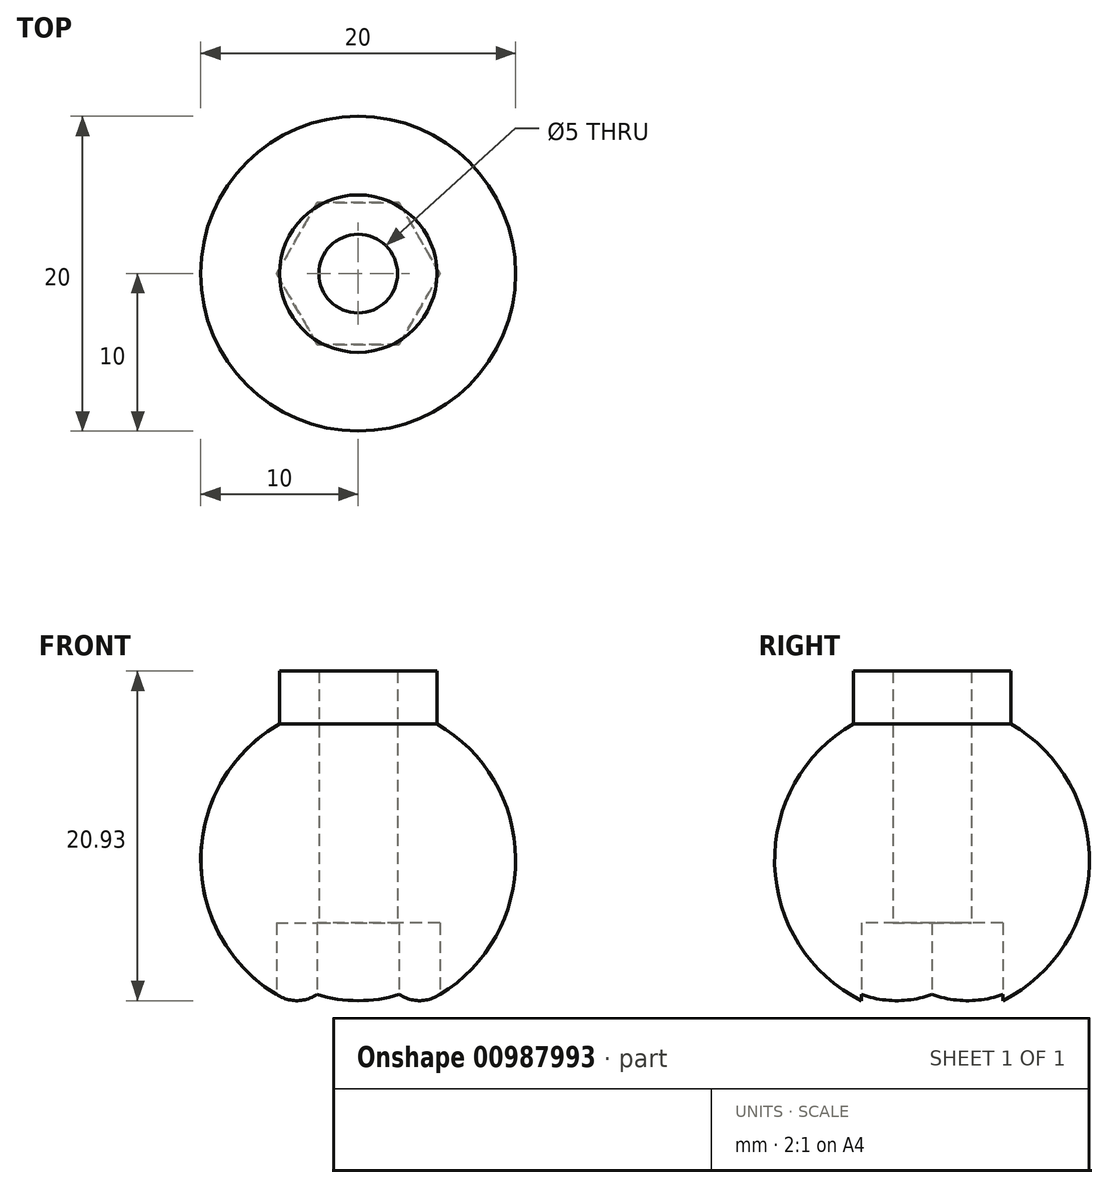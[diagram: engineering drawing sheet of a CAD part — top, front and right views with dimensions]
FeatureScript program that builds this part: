
annotation { "Feature Type Name" : "Feature", "Feature Type Description" : "" }
export const myFeature = defineFeature(function(context is Context, id is Id, definition is map)
    precondition{}
    {
        {
            var Q0;
            Q0=qCreatedBy(makeId("Front.planeOp"),FACE);
            var sketch = newSketch(context, id + "F0", { "sketchPlane" : qUnion([Q0])});
            skLineSegment(sketch, "E0", {"start": v(0, 20) * mm, "end": v(0, 20) * mm});
            skLineSegment(sketch, "E1", {"start": v(0, 20) * mm, "end": v(0, 0) * mm});
            skLineSegment(sketch, "E2", {"start": v(0, 0) * mm, "end": v(0, 0) * mm});
            skArc(sketch, "E3", {"start": v(0, 0) * mm, "mid": v(10, 10) * mm, "end": v(0, 20) * mm});
            skSolve(sketch);
        }
        {
            var Q0;
            Q0 = qSketchRegion(id + "F0", true);
            var Q1;
            Q1=sQuery(id+"F0.wireOp",EDGE,"E1");
            revolve(context, id + "F1", {"surfaceOperationType" : NewSurfaceOperationType.NEW, "entities" : qUnion([Q0]), "axis" : qUnion([Q1]), "revolveType" : RevolveType.FULL});
        }
        {
            var Q0;
            Q0=qCreatedBy(makeId("Top.planeOp"),FACE);
            var sketch = newSketch(context, id + "F2", { "sketchPlane" : qUnion([Q0])});
            skCircle(sketch, "E4.cCircle", {"center": v(0, 0) * mm, "radius": 4.5 * mm, "construction": true});
            skLineSegment(sketch, "E4.0", {"start": v(2.6, -4.5) * mm, "end": v(-2.6, -4.5) * mm});
            skLineSegment(sketch, "E4.1", {"start": v(-2.6, -4.5) * mm, "end": v(-5.2, 0) * mm});
            skLineSegment(sketch, "E4.2", {"start": v(-5.2, 0) * mm, "end": v(-2.6, 4.5) * mm});
            skLineSegment(sketch, "E4.3", {"start": v(-2.6, 4.5) * mm, "end": v(2.6, 4.5) * mm});
            skLineSegment(sketch, "E4.4", {"start": v(2.6, 4.5) * mm, "end": v(5.2, 0) * mm});
            skLineSegment(sketch, "E4.5", {"start": v(5.2, 0) * mm, "end": v(2.6, -4.5) * mm});
            skPoint(sketch, "E4.0.midPoint", {"position": v(0, -4.5) * mm});
            skSolve(sketch);
        }
        {
            var Q0;
            Q0 = qSketchRegion(id + "F2", true);
            extrude(context, id + "F3", {"entities" : qUnion([Q0]), "operationType" : NewBodyOperationType.REMOVE, "depth" : 6 * mm, "offsetDistance" : 25 * mm});
        }
        {
            var Q0;
            Q0=makeQuery(id+"F3.boolean.opBoolean","COPY",FACE,{"derivedFrom":makeQuery(id+"F3.opExtrude","CAP_FACE",FACE,{"disambiguationData":[OSD([sQuery(id+"F2.wireOp",EDGE,"E4.0"),sQuery(id+"F2.wireOp",EDGE,"E4.1"),sQuery(id+"F2.wireOp",EDGE,"E4.2"),sQuery(id+"F2.wireOp",EDGE,"E4.3"),sQuery(id+"F2.wireOp",EDGE,"E4.4"),sQuery(id+"F2.wireOp",EDGE,"E4.5")])],"isStart":false})});
            var sketch = newSketch(context, id + "F4", { "sketchPlane" : qUnion([Q0])});
            skCircle(sketch, "E5", {"center": v(0, 0) * mm, "radius": 5 * mm});
            skSolve(sketch);
        }
        {
            var Q0;
            Q0 = qSketchRegion(id + "F4", true);
            extrude(context, id + "F5", {"entities" : qUnion([Q0]), "operationType" : NewBodyOperationType.ADD, "oppositeDirection" : true, "depth" : 16 * mm, "offsetDistance" : 25 * mm});
        }
        {
            var Q0;
            Q0=makeQuery(id+"F3.boolean.opBoolean","COPY",FACE,{"derivedFrom":makeQuery(id+"F3.opExtrude","CAP_FACE",FACE,{"disambiguationData":[OSD([sQuery(id+"F2.wireOp",EDGE,"E4.0"),sQuery(id+"F2.wireOp",EDGE,"E4.1"),sQuery(id+"F2.wireOp",EDGE,"E4.2"),sQuery(id+"F2.wireOp",EDGE,"E4.3"),sQuery(id+"F2.wireOp",EDGE,"E4.4"),sQuery(id+"F2.wireOp",EDGE,"E4.5")])],"isStart":false})});
            var sketch = newSketch(context, id + "F6", { "sketchPlane" : qUnion([Q0])});
            skCircle(sketch, "E6", {"center": v(0, 0) * mm, "radius": 2.5 * mm});
            skSolve(sketch);
        }
        {
            var Q0;
            Q0 = qSketchRegion(id + "F6", true);
            extrude(context, id + "F7", {"entities" : qUnion([Q0]), "operationType" : NewBodyOperationType.REMOVE, "oppositeDirection" : true, "depth" : 25 * mm, "offsetDistance" : 25 * mm});
        }
    });
